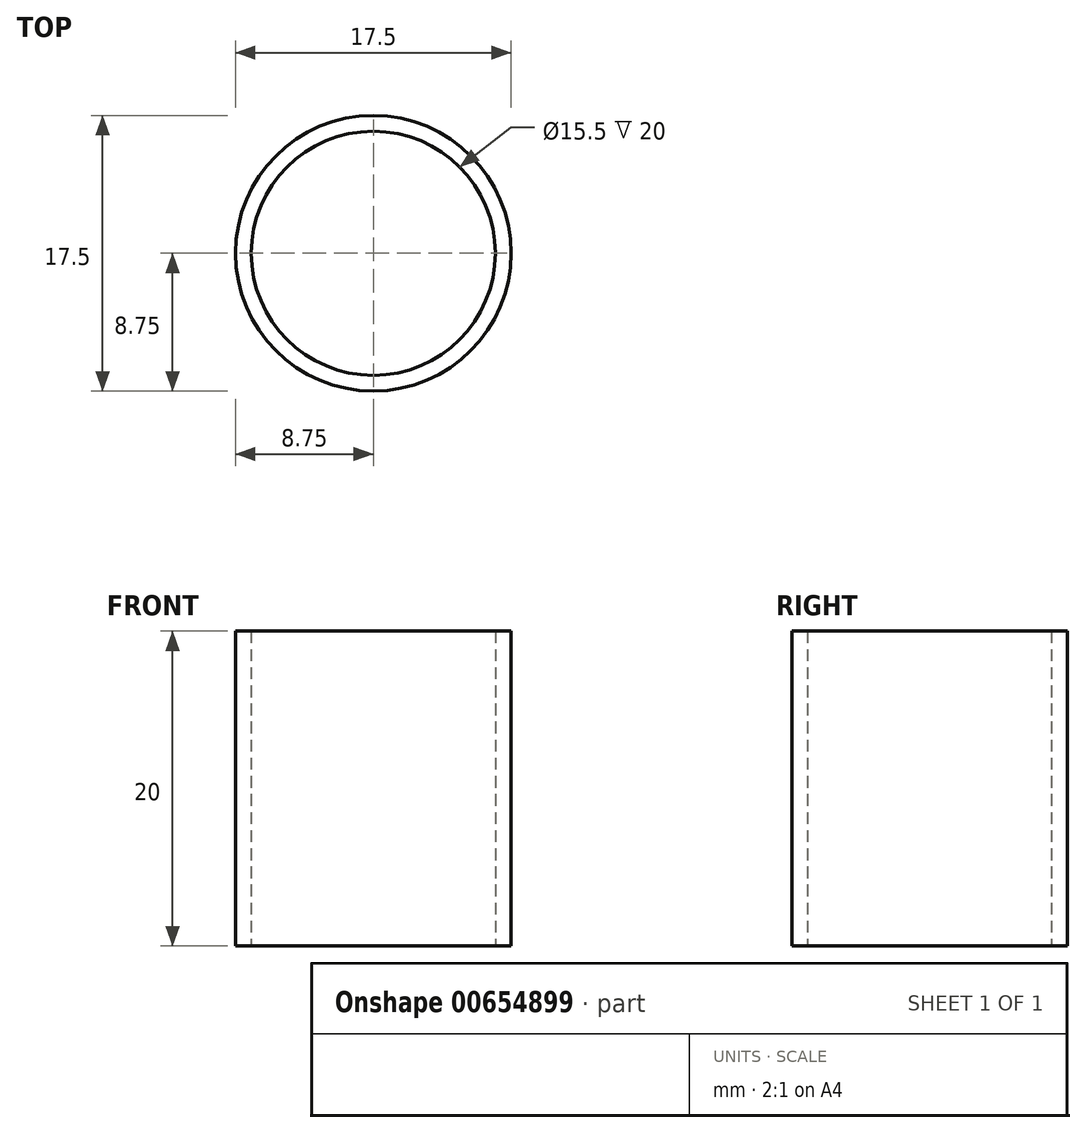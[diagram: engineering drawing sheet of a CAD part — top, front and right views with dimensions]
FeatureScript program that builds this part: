
annotation { "Feature Type Name" : "Feature", "Feature Type Description" : "" }
export const myFeature = defineFeature(function(context is Context, id is Id, definition is map)
    precondition{}
    {
        {
            var Q0;
            Q0=qCreatedBy(makeId("Top.planeOp"),FACE);
            var sketch = newSketch(context, id + "F0", { "sketchPlane" : qUnion([Q0])});
            skCircle(sketch, "E0", {"center": v(0, 0) * mm, "radius": 7.75 * mm});
            skCircle(sketch, "E1", {"center": v(0, 0) * mm, "radius": 8.75 * mm});
            skSolve(sketch);
        }
        {
            var Q0;
            Q0=makeQuery(id+"F0.imprint","IMPRINT",FACE,{"disambiguationData":[TD([[makeQuery(id+"F0.imprint","IMPRINT",EDGE,{"derivedFrom":sQuery(id+"F0.wireOp",EDGE,"E0")}),-1.0]])]});
            extrude(context, id + "F1", {"entities" : qUnion([Q0]), "depth" : 20 * mm, "offsetDistance" : 25 * mm});
        }
    });
